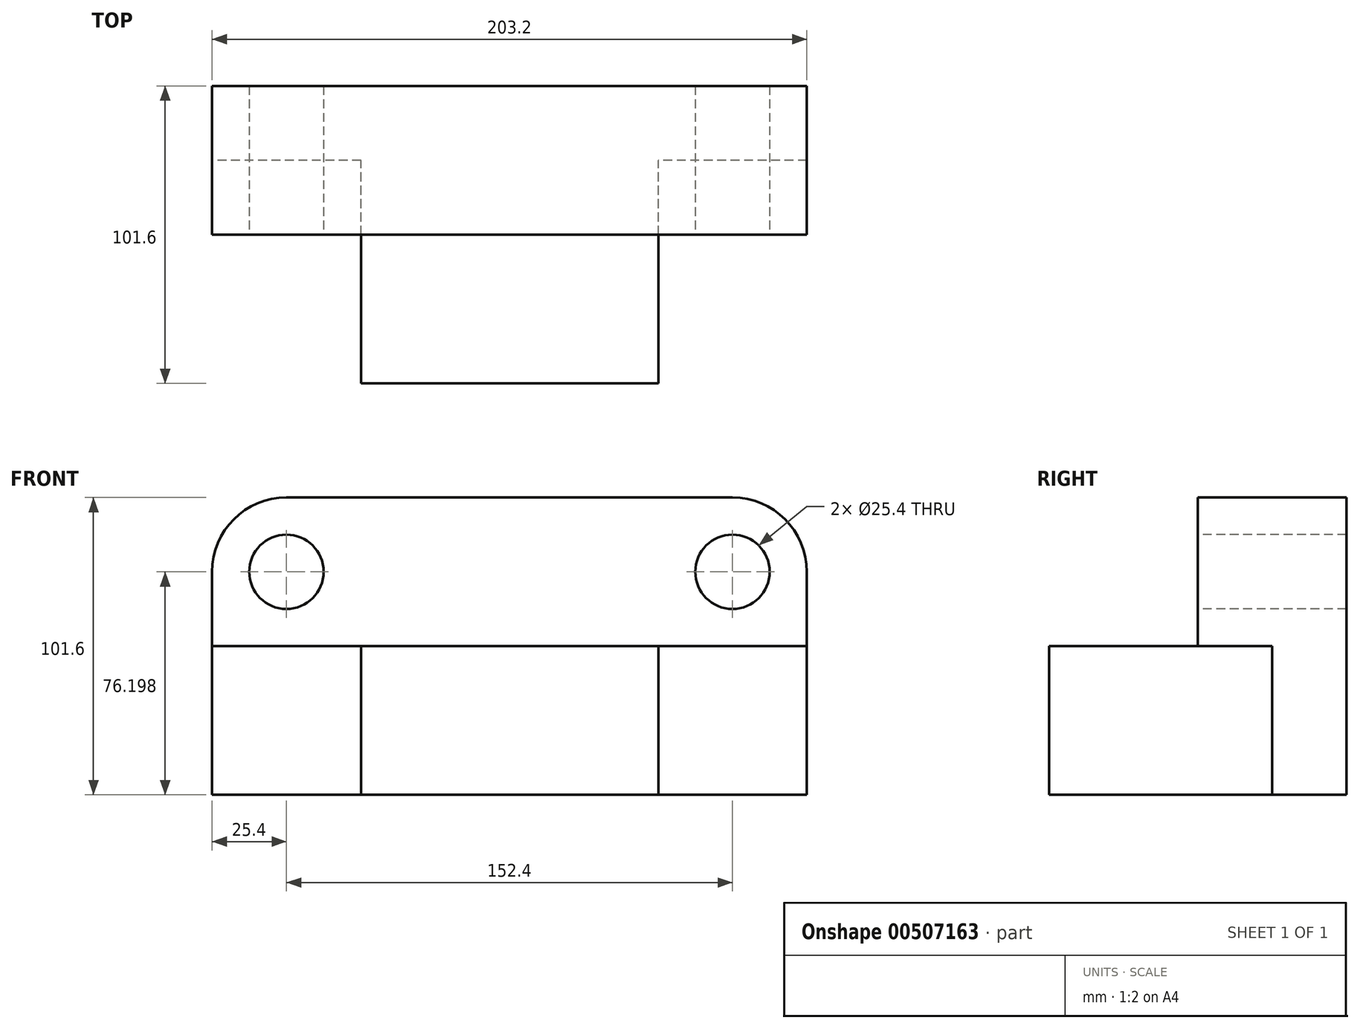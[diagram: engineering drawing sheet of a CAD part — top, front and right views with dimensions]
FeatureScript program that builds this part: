
annotation { "Feature Type Name" : "Feature", "Feature Type Description" : "" }
export const myFeature = defineFeature(function(context is Context, id is Id, definition is map)
    precondition{}
    {
        {
            var Q0;
            Q0=qCreatedBy(makeId("Right.planeOp"),FACE);
            var sketch = newSketch(context, id + "F0", { "sketchPlane" : qUnion([Q0])});
            skLineSegment(sketch, "E0", {"start": v(-19.48, 27.2) * mm, "end": v(31.32, 27.2) * mm});
            skLineSegment(sketch, "E1", {"start": v(31.32, 27.2) * mm, "end": v(31.32, -49) * mm});
            skLineSegment(sketch, "E2", {"start": v(31.32, -49) * mm, "end": v(5.92, -49) * mm});
            skLineSegment(sketch, "E3", {"start": v(5.92, -49) * mm, "end": v(5.92, 1.8) * mm});
            skLineSegment(sketch, "E4", {"start": v(5.92, 1.8) * mm, "end": v(-19.48, 1.8) * mm});
            skLineSegment(sketch, "E5", {"start": v(-19.48, 1.8) * mm, "end": v(-19.48, 27.2) * mm});
            skSolve(sketch);
        }
        {
            var Q0;
            Q0 = qSketchRegion(id + "F0", true);
            extrude(context, id + "F1", {"entities" : qUnion([Q0]), "depth" : 203.2 * mm, "offsetDistance" : 25.4 * mm});
        }
        {
            var Q0;
            Q0=makeQuery(id+"F1.opExtrude","SWEPT_FACE",FACE,{"disambiguationData":[OSD([sQuery(id+"F0.wireOp",EDGE,"E3")])]});
            var sketch = newSketch(context, id + "F2", { "sketchPlane" : qUnion([Q0])});
            skLineSegment(sketch, "E6", {"start": v(50.92, -49) * mm, "end": v(152.52, -49) * mm});
            skLineSegment(sketch, "E7", {"start": v(152.52, -49) * mm, "end": v(152.52, 1.8) * mm});
            skLineSegment(sketch, "E8", {"start": v(152.52, 1.8) * mm, "end": v(50.92, 1.8) * mm});
            skLineSegment(sketch, "E9", {"start": v(50.92, 1.8) * mm, "end": v(50.92, -49) * mm});
            skSolve(sketch);
        }
        {
            var Q0;
            Q0 = qSketchRegion(id + "F2", true);
            extrude(context, id + "F3", {"entities" : qUnion([Q0]), "operationType" : NewBodyOperationType.ADD, "depth" : 76.2 * mm, "offsetDistance" : 25.4 * mm});
        }
        {
            var Q0;
            Q0=makeQuery(id+"F1.opExtrude","SWEPT_FACE",FACE,{"disambiguationData":[OSD([sQuery(id+"F0.wireOp",EDGE,"E5")])]});
            var sketch = newSketch(context, id + "F4", { "sketchPlane" : qUnion([Q0])});
            skLineSegment(sketch, "E10", {"start": v(0, 27.2) * mm, "end": v(0, 52.6) * mm});
            skLineSegment(sketch, "E11", {"start": v(0, 52.6) * mm, "end": v(203.2, 52.6) * mm});
            skLineSegment(sketch, "E12", {"start": v(203.2, 52.6) * mm, "end": v(203.2, 27.2) * mm});
            skLineSegment(sketch, "E13", {"start": v(203.2, 27.2) * mm, "end": v(0, 27.2) * mm});
            skSolve(sketch);
        }
        {
            var Q0;
            Q0 = qSketchRegion(id + "F4", true);
            extrude(context, id + "F5", {"entities" : qUnion([Q0]), "operationType" : NewBodyOperationType.ADD, "oppositeDirection" : true, "depth" : 50.8 * mm, "offsetDistance" : 25.4 * mm});
        }
        {
            var Q0;
            Q0=makeQuery(id+"F5.opExtrude","SWEPT_EDGE",EDGE,{"disambiguationData":[OSD([sQuery(id+"F4.wireOp",EDGE,"E10"),sQuery(id+"F4.wireOp",EDGE,"E11")])]});
            var Q1;
            Q1=makeQuery(id+"F5.opExtrude","SWEPT_EDGE",EDGE,{"disambiguationData":[OSD([sQuery(id+"F4.wireOp",EDGE,"E11"),sQuery(id+"F4.wireOp",EDGE,"E12")])]});
            fillet(context, id + "F6", {"entities" : qUnion([Q0, Q1]), "radius" : 25.4 * mm, "tangentPropagation" : true, "allowEdgeOverflow" : false});
        }
        {
            var Q0;
            Q0=makeQuery(id+"F5.boolean.opBoolean","MERGE",FACE,{"derivedFrom":[makeQuery(id+"F1.opExtrude","SWEPT_FACE",FACE,{"disambiguationData":[OSD([sQuery(id+"F0.wireOp",EDGE,"E5")])]}),makeQuery(id+"F5.opExtrude","CAP_FACE",FACE,{"disambiguationData":[OSD([sQuery(id+"F4.wireOp",EDGE,"E10"),sQuery(id+"F4.wireOp",EDGE,"E11"),sQuery(id+"F4.wireOp",EDGE,"E12"),sQuery(id+"F4.wireOp",EDGE,"E13")])],"isStart":true})]});
            var sketch = newSketch(context, id + "F7", { "sketchPlane" : qUnion([Q0])});
            skCircle(sketch, "E14", {"center": v(25.4, 27.2) * mm, "radius": 12.7 * mm});
            skSolve(sketch);
        }
        {
            var Q0;
            Q0=makeQuery(id+"F7.imprint","IMPRINT",FACE,{"disambiguationData":[TD([[makeQuery(id+"F7.imprint","IMPRINT",EDGE,{"derivedFrom":sQuery(id+"F7.wireOp",EDGE,"E14")}),-1.0]])]});
            var sketch = newSketch(context, id + "F8", { "sketchPlane" : qUnion([Q0])});
            skCircle(sketch, "E15", {"center": v(177.8, 27.2) * mm, "radius": 12.7 * mm});
            skSolve(sketch);
        }
        {
            var Q0;
            Q0=sQuery(id+"F7.wireOp",VERTEX,"E14.center");
            var Q1;
            Q1=sQuery(id+"F8.wireOp",VERTEX,"E15.center");
            var Q2;
            Q2=makeQuery(id+"F1.opExtrude","SWEPT_BODY",BODY,{"disambiguationData":[OSD([sQuery(id+"F0.wireOp",EDGE,"E0"),sQuery(id+"F0.wireOp",EDGE,"E1"),sQuery(id+"F0.wireOp",EDGE,"E2"),sQuery(id+"F0.wireOp",EDGE,"E3"),sQuery(id+"F0.wireOp",EDGE,"E4"),sQuery(id+"F0.wireOp",EDGE,"E5")])]});
            hole(context, id + "F9", {"style" : HoleStyle.SIMPLE, "endStyle" : HoleEndStyle.THROUGH, "holeDiameter" : 25.4 * mm, "isTappedThrough" : true, "tappedDepth" : 12.7 * mm, "tapClearance" : 3, "locations" : qUnion([Q0, Q1]), "scope" : qUnion([Q2])});
        }
    });
